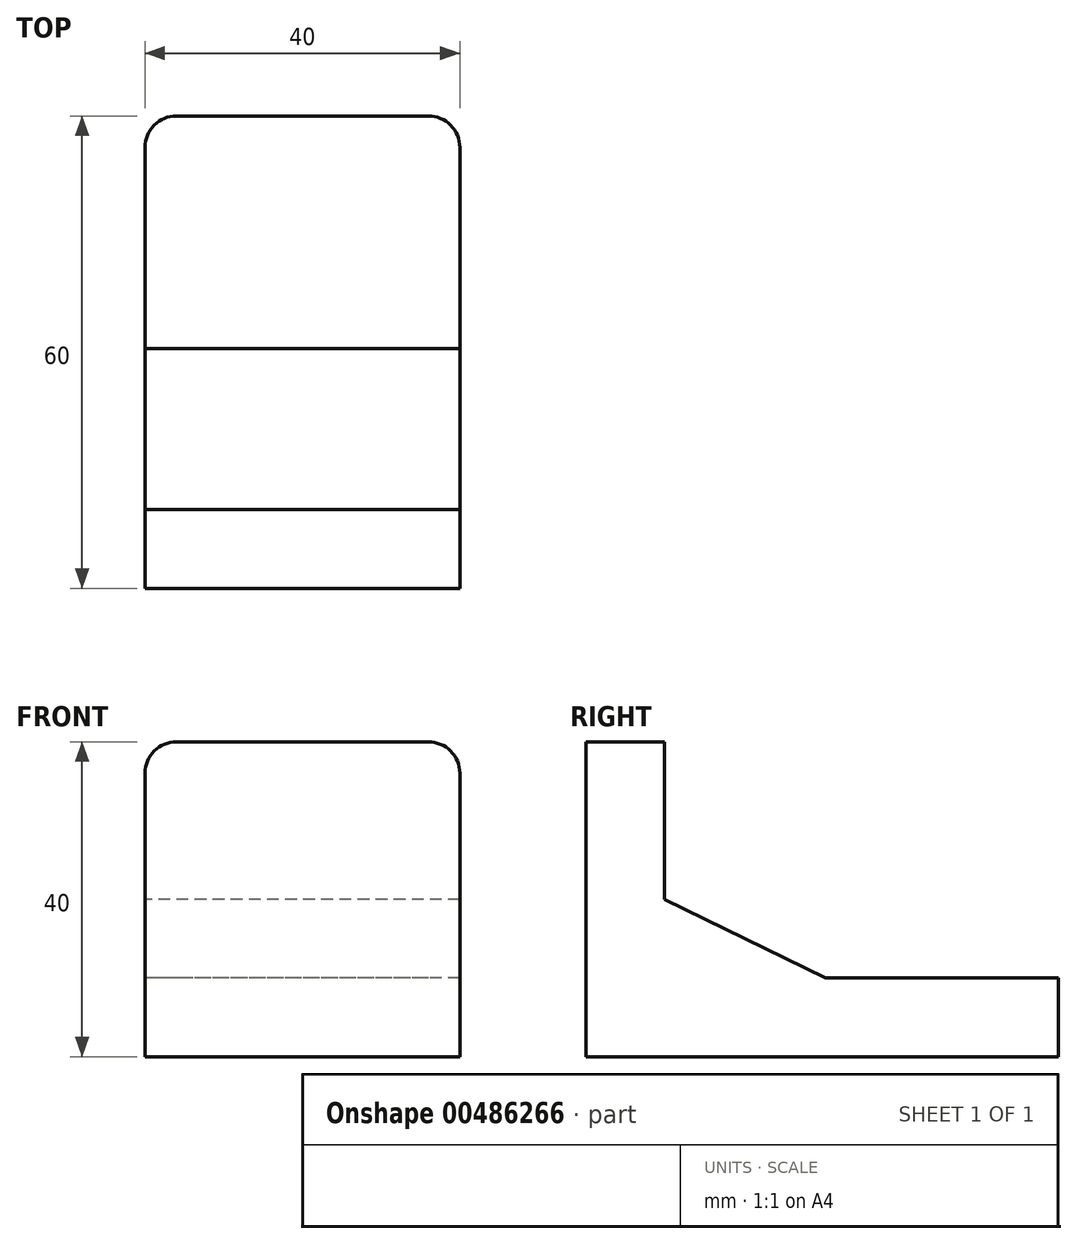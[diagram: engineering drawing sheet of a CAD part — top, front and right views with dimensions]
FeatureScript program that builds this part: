
annotation { "Feature Type Name" : "Feature", "Feature Type Description" : "" }
export const myFeature = defineFeature(function(context is Context, id is Id, definition is map)
    precondition{}
    {
        {
            var Q0;
            Q0=qCreatedBy(makeId("Right.planeOp"),FACE);
            var sketch = newSketch(context, id + "F0", { "sketchPlane" : qUnion([Q0])});
            skLineSegment(sketch, "E0.top", {"start": v(-32.28, -20) * mm, "end": v(27.72, -20) * mm});
            skLineSegment(sketch, "E0.left", {"start": v(-32.28, 20) * mm, "end": v(-32.28, -20) * mm});
            skLineSegment(sketch, "E1", {"start": v(-32.28, 20) * mm, "end": v(-22.28, 20) * mm});
            skLineSegment(sketch, "E2", {"start": v(-22.28, 20) * mm, "end": v(-22.28, 0) * mm});
            skLineSegment(sketch, "E3", {"start": v(-1.82, -10) * mm, "end": v(27.72, -10) * mm});
            skLineSegment(sketch, "E4", {"start": v(27.72, -20) * mm, "end": v(27.72, -10) * mm});
            skLineSegment(sketch, "E5", {"start": v(-22.28, 0) * mm, "end": v(-1.82, -10) * mm});
            skPoint(sketch, "E6.end.orphan", {"position": v(-31.37, -10) * mm});
            skSolve(sketch);
        }
        {
            var Q0;
            Q0=makeQuery(id+"F0.imprint","IMPRINT",FACE,{"disambiguationData":[TD([[makeQuery(id+"F0.imprint","IMPRINT",EDGE,{"derivedFrom":sQuery(id+"F0.wireOp",EDGE,"E0.top")}),1.0]])]});
            extrude(context, id + "F1", {"entities" : qUnion([Q0]), "depth" : 40 * mm});
        }
        {
            var Q0;
            Q0=makeQuery(id+"F1.opExtrude","CAP_EDGE",EDGE,{"disambiguationData":[OSD([sQuery(id+"F0.wireOp",EDGE,"E1")])],"isStart":false});
            var Q1;
            Q1=makeQuery(id+"F1.opExtrude","CAP_EDGE",EDGE,{"disambiguationData":[OSD([sQuery(id+"F0.wireOp",EDGE,"E1")])],"isStart":true});
            var Q2;
            Q2=makeQuery(id+"F1.opExtrude","CAP_EDGE",EDGE,{"disambiguationData":[OSD([sQuery(id+"F0.wireOp",EDGE,"E4")])],"isStart":false});
            var Q3;
            Q3=makeQuery(id+"F1.opExtrude","CAP_EDGE",EDGE,{"disambiguationData":[OSD([sQuery(id+"F0.wireOp",EDGE,"E4")])],"isStart":true});
            fillet(context, id + "F2", {"entities" : qUnion([Q0, Q1, Q2, Q3]), "radius" : 4 * mm, "tangentPropagation" : true, "allowEdgeOverflow" : false});
        }
    });
